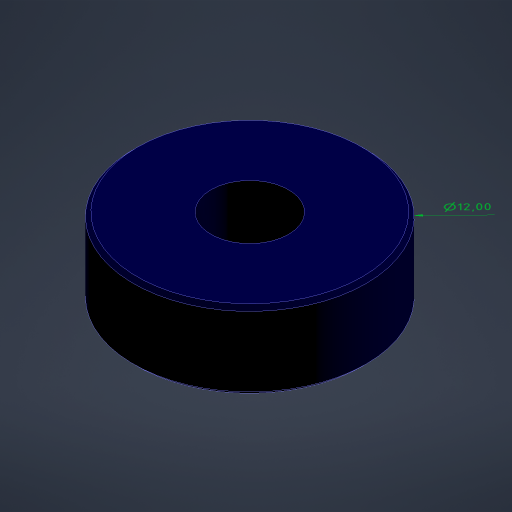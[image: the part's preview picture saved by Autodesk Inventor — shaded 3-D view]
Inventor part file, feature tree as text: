
AUTODESK INVENTOR PART (.ipt)
format: ipt  version: 2024 (Build 280153000, 153)  size: 184,320 bytes
history: native  units: mm
features: other x3, extrude x1, chamfer x1, sketch x1
ambient origin geometry x8: Origin, YZ Plane, XZ Plane, XY Plane, X Axis, Y Axis, Z Axis, Center Point
bodies: Body1 (feature_tree)
feature tree (6):
  other  "Твердое тело1"
  other  "Аннотации"
  extrude  "Выдавливание1"  Depth=12.0mm
  chamfer  "Фаска1"  Distance=4.0mm
  sketch  "Эскиз1"
  other  "Диаметр 1"
